# Revit family: Panel_Hinge-RadiusCorner_CastleAccess
name_source: partatom
category: Generic Models
units: mm (PartAtom-declared; Revit-internal decimal feet)

## family parameters
Can host rebar = No
Cut with Voids When Loaded = Yes
Host = Face
Maintain Annotation Orientation = No
Part Type = Normal
Room Calculation Point = No
Round Connector Dimension = Use Diameter
Shared = No

## types (1)
- Panel_Hinge-RadiusCorner_CastleAccess
    Access Opening Height = 5"
    Access Opening Width = 8"
    Assembly Code = C3030140
    Cam Latch Quantity = 0
    Clearance Depth = 8"
    Construction Details = http://www.arcat.com
    Cost = 0 $
    Default Elevation = 0"
    Expected Lifespan (Years) = 0
    Green Building-LEED = http://www.arcat.com
    Hinge Quantity = 0
    Installation Phase = Ceiling Finishes - Paneling
    Keynote = 09 54 53
    Manufacturer = Castle Access Panels & Forms Inc.
    Manufacturer Fax = (+1)905-760-9234
    Manufacturer Website = https://www.castleaccesspanels.com
    Model = As Specified
    Product Data = http://www.arcat.com
    Product Properties = http://www.arcat.com
    Revision = R0_2018-01
    Sales Information = https://www.castleaccesspanels.com
    Send Message = https://www.castleaccesspanels.com
    Specification = https://www.castleaccesspanels.com
    Standards Conformance = as Specified
    Test Data = https://www.castleaccesspanels.com
    URL = http://www.arcat.com
    Unit Area = 0.28 SF
    Unit Depth = 5/8"
    Unit Height = 0"
    Unit Weight = 0
    Warranty Duration (Years) = 3

## geometry (parser evidence)
native form markers: Sweep x2
no freeform markers — native parametric forms only
